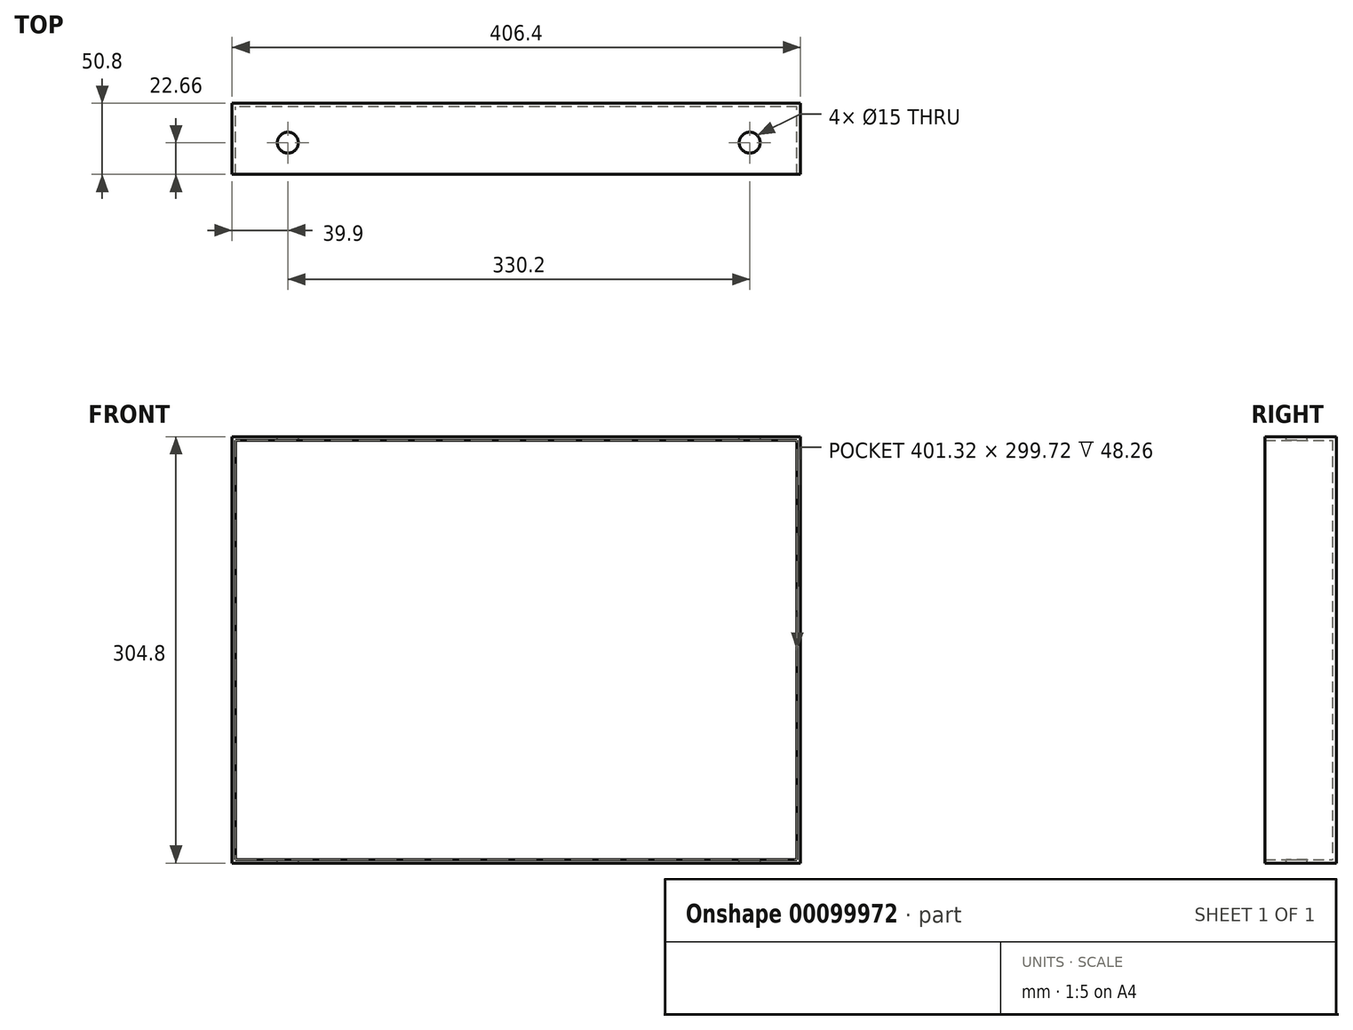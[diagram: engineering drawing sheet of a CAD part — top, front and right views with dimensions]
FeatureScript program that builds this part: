
annotation { "Feature Type Name" : "Feature", "Feature Type Description" : "" }
export const myFeature = defineFeature(function(context is Context, id is Id, definition is map)
    precondition{}
    {
        {
            var Q0;
            Q0=qCreatedBy(makeId("Front.planeOp"),FACE);
            var sketch = newSketch(context, id + "F0", { "sketchPlane" : qUnion([Q0])});
            skLineSegment(sketch, "E0.bottom", {"start": v(201.4, 152.4) * mm, "end": v(-205, 152.4) * mm});
            skLineSegment(sketch, "E0.top", {"start": v(201.4, -152.4) * mm, "end": v(-205, -152.4) * mm});
            skLineSegment(sketch, "E0.left", {"start": v(201.4, 152.4) * mm, "end": v(201.4, -152.4) * mm});
            skLineSegment(sketch, "E0.right", {"start": v(-205, 152.4) * mm, "end": v(-205, -152.4) * mm});
            skPoint(sketch, "E0.middle", {"position": v(-1.8, 0) * mm});
            skSolve(sketch);
        }
        {
            var Q0;
            Q0 = qSketchRegion(id + "F0", true);
            extrude(context, id + "F1", {"entities" : qUnion([Q0]), "depth" : 50.8 * mm});
        }
        {
            var Q0;
            Q0=makeQuery(id+"F1.opExtrude","CAP_FACE",FACE,{"disambiguationData":[OSD([sQuery(id+"F0.wireOp",EDGE,"E0.bottom"),sQuery(id+"F0.wireOp",EDGE,"E0.top"),sQuery(id+"F0.wireOp",EDGE,"E0.left"),sQuery(id+"F0.wireOp",EDGE,"E0.right")])],"isStart":false});
            shell(context, id + "F2", {"entities" : qUnion([Q0]), "thickness" : 2.54 * mm});
        }
        {
            var Q0;
            Q0=makeQuery(id+"F1.opExtrude","SWEPT_FACE",FACE,{"disambiguationData":[OSD([sQuery(id+"F0.wireOp",EDGE,"E0.bottom")])]});
            var sketch = newSketch(context, id + "F3", { "sketchPlane" : qUnion([Q0])});
            skLineSegment(sketch, "E1", {"start": v(-205, 0) * mm, "end": v(-205, -50.8) * mm});
            skSolve(sketch);
        }
        {
            var Q0;
            {var subQ0=sQuery(id+"F0.wireOp",EDGE,"E0.bottom");Q0=makeQuery(id+"F3.imprint","IMPRINT",FACE,{"disambiguationData":[TD([[makeQuery(id+"F3.imprint","IMPRINT",EDGE,{"derivedFrom":makeQuery(id+"F1.opExtrude","CAP_EDGE",EDGE,{"disambiguationData":[OSD([subQ0])],"isStart":true})}),1.0]])]});}
            var sketch = newSketch(context, id + "F4", { "sketchPlane" : qUnion([Q0])});
            skLineSegment(sketch, "E2", {"start": v(0, -28.14) * mm, "end": v(165.1, -28.14) * mm});
            skLineSegment(sketch, "E3", {"start": v(0, -28.14) * mm, "end": v(-165.1, -28.14) * mm});
            skPoint(sketch, "E4", {"position": v(-165.1, -28.14) * mm});
            skPoint(sketch, "E5", {"position": v(165.1, -28.14) * mm});
            skSolve(sketch);
        }
        {
            var Q0;
            Q0=sQuery(id+"F4.wireOp",VERTEX,"E4");
            var Q1;
            Q1=sQuery(id+"F4.wireOp",VERTEX,"E5");
            var Q2;
            Q2=makeQuery(id+"F1.opExtrude","SWEPT_BODY",BODY,{"disambiguationData":[OSD([sQuery(id+"F0.wireOp",EDGE,"E0.bottom"),sQuery(id+"F0.wireOp",EDGE,"E0.top"),sQuery(id+"F0.wireOp",EDGE,"E0.left"),sQuery(id+"F0.wireOp",EDGE,"E0.right")])]});
            hole(context, id + "F5", {"style" : HoleStyle.SIMPLE, "endStyle" : HoleEndStyle.THROUGH, "holeDiameter" : 15 * mm, "locations" : qUnion([Q0, Q1]), "scope" : qUnion([Q2]), "isTappedThrough" : true});
        }
    });
